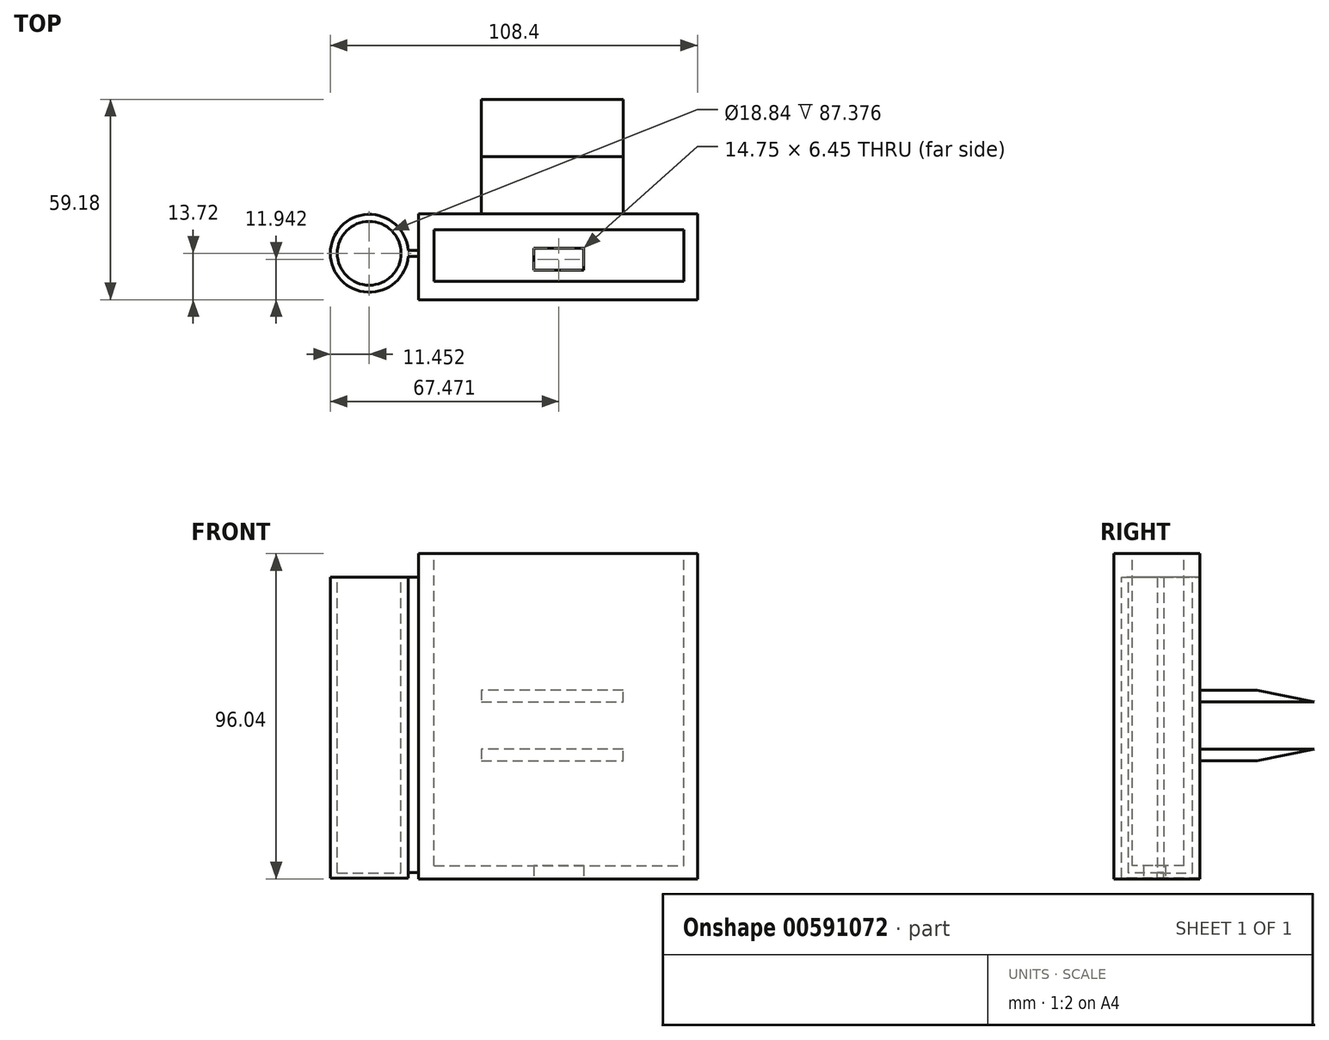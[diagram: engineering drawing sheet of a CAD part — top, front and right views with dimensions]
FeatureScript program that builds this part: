
annotation { "Feature Type Name" : "Feature", "Feature Type Description" : "" }
export const myFeature = defineFeature(function(context is Context, id is Id, definition is map)
    precondition{}
    {
        {
            var Q0;
            Q0=qCreatedBy(makeId("Front.planeOp"),FACE);
            var sketch = newSketch(context, id + "F0", { "sketchPlane" : qUnion([Q0])});
            skLineSegment(sketch, "E0.bottom", {"start": v(-39.73, 43.78) * mm, "end": v(42.68, 43.78) * mm});
            skLineSegment(sketch, "E0.top", {"start": v(-39.73, -52.26) * mm, "end": v(42.68, -52.26) * mm});
            skLineSegment(sketch, "E0.left", {"start": v(-39.73, 43.78) * mm, "end": v(-39.73, -52.26) * mm});
            skLineSegment(sketch, "E0.right", {"start": v(42.68, 43.78) * mm, "end": v(42.68, -52.26) * mm});
            skSolve(sketch);
        }
        {
            var Q0;
            Q0 = qSketchRegion(id + "F0", true);
            extrude(context, id + "F1", {"entities" : qUnion([Q0]), "depth" : 25.4 * mm, "offsetDistance" : 25.4 * mm});
        }
        {
            var Q0;
            Q0=makeQuery(id+"F1.opExtrude","SWEPT_FACE",FACE,{"disambiguationData":[OSD([sQuery(id+"F0.wireOp",EDGE,"E0.bottom")])]});
            var sketch = newSketch(context, id + "F2", { "sketchPlane" : qUnion([Q0])});
            skLineSegment(sketch, "E1.bottom", {"start": v(-35.12, -4.7) * mm, "end": v(38.62, -4.7) * mm});
            skLineSegment(sketch, "E1.top", {"start": v(-35.12, -20) * mm, "end": v(38.62, -20) * mm});
            skLineSegment(sketch, "E1.left", {"start": v(-35.12, -4.7) * mm, "end": v(-35.12, -20) * mm});
            skLineSegment(sketch, "E1.right", {"start": v(38.62, -4.7) * mm, "end": v(38.62, -20) * mm});
            skSolve(sketch);
        }
        {
            var Q0;
            Q0 = qSketchRegion(id + "F2", true);
            extrude(context, id + "F3", {"entities" : qUnion([Q0]), "operationType" : NewBodyOperationType.REMOVE, "oppositeDirection" : true, "depth" : 92.2 * mm, "offsetDistance" : 25.4 * mm});
        }
        {
            var Q0;
            Q0=makeQuery(id+"F1.opExtrude","CAP_FACE",FACE,{"disambiguationData":[OSD([sQuery(id+"F0.wireOp",EDGE,"E0.bottom"),sQuery(id+"F0.wireOp",EDGE,"E0.top"),sQuery(id+"F0.wireOp",EDGE,"E0.left"),sQuery(id+"F0.wireOp",EDGE,"E0.right")])],"isStart":true});
            var sketch = newSketch(context, id + "F4", { "sketchPlane" : qUnion([Q0])});
            skLineSegment(sketch, "E2", {"start": v(-20.74, 3.5) * mm, "end": v(21.1, 3.5) * mm});
            skLineSegment(sketch, "E3", {"start": v(21.1, 3.5) * mm, "end": v(21.1, 0) * mm});
            skLineSegment(sketch, "E4", {"start": v(21.1, 0) * mm, "end": v(-20.74, 0) * mm});
            skLineSegment(sketch, "E5", {"start": v(-20.74, 0) * mm, "end": v(-20.74, 3.5) * mm});
            skLineSegment(sketch, "E6", {"start": v(-20.74, -13.92) * mm, "end": v(21.1, -13.92) * mm});
            skLineSegment(sketch, "E7", {"start": v(21.1, -13.92) * mm, "end": v(21.1, -17.42) * mm});
            skLineSegment(sketch, "E8", {"start": v(21.1, -17.42) * mm, "end": v(-20.74, -17.42) * mm});
            skLineSegment(sketch, "E9", {"start": v(-20.74, -17.42) * mm, "end": v(-20.74, -13.92) * mm});
            skSolve(sketch);
        }
        {
            var Q0;
            Q0 = qSketchRegion(id + "F4", true);
            extrude(context, id + "F5", {"entities" : qUnion([Q0]), "operationType" : NewBodyOperationType.ADD, "depth" : 33.78 * mm, "offsetDistance" : 25.4 * mm});
        }
        {
            var Q0;
            Q0=makeQuery(id+"F5.opExtrude","SWEPT_FACE",FACE,{"disambiguationData":[OSD([sQuery(id+"F4.wireOp",EDGE,"E5")])]});
            var sketch = newSketch(context, id + "F6", { "sketchPlane" : qUnion([Q0])});
            skLineSegment(sketch, "E10", {"start": v(0, 3.5) * mm, "end": v(16.9, 3.5) * mm});
            skLineSegment(sketch, "E11", {"start": v(16.9, 3.5) * mm, "end": v(33.78, 0) * mm});
            skSolve(sketch);
        }
        {
            var Q0;
            {var subQ0=sQuery(id+"F6.wireOp",EDGE,"E11");Q0=makeQuery(id+"F6.imprint","IMPRINT",FACE,{"disambiguationData":[TD([[makeQuery(id+"F6.imprint","IMPRINT",EDGE,{"derivedFrom":subQ0}),1.0]])]});}
            extrude(context, id + "F7", {"entities" : qUnion([Q0]), "operationType" : NewBodyOperationType.REMOVE, "oppositeDirection" : true, "depth" : 58.93 * mm, "offsetDistance" : 25.4 * mm});
        }
        {
            var Q0;
            Q0=makeQuery(id+"F5.opExtrude","SWEPT_FACE",FACE,{"disambiguationData":[OSD([sQuery(id+"F4.wireOp",EDGE,"E9")])]});
            var sketch = newSketch(context, id + "F8", { "sketchPlane" : qUnion([Q0])});
            skLineSegment(sketch, "E12", {"start": v(0, -17.42) * mm, "end": v(16.9, -17.42) * mm});
            skLineSegment(sketch, "E13", {"start": v(16.9, -17.42) * mm, "end": v(33.78, -13.92) * mm});
            skSolve(sketch);
        }
        {
            var Q0;
            {var subQ0=sQuery(id+"F8.wireOp",EDGE,"E13");Q0=makeQuery(id+"F8.imprint","IMPRINT",FACE,{"disambiguationData":[TD([[makeQuery(id+"F8.imprint","IMPRINT",EDGE,{"derivedFrom":subQ0}),-1.0]])]});}
            extrude(context, id + "F9", {"entities" : qUnion([Q0]), "operationType" : NewBodyOperationType.REMOVE, "oppositeDirection" : true, "depth" : 50.3 * mm, "offsetDistance" : 25.4 * mm});
        }
        {
            var Q0;
            Q0=makeQuery(id+"F1.opExtrude","SWEPT_FACE",FACE,{"disambiguationData":[OSD([sQuery(id+"F0.wireOp",EDGE,"E0.top")])]});
            var sketch = newSketch(context, id + "F10", { "sketchPlane" : qUnion([Q0])});
            skLineSegment(sketch, "E14.bottom", {"start": v(-5.62, 16.68) * mm, "end": v(9.13, 16.68) * mm});
            skLineSegment(sketch, "E14.top", {"start": v(-5.62, 10.23) * mm, "end": v(9.13, 10.23) * mm});
            skLineSegment(sketch, "E14.left", {"start": v(-5.62, 16.68) * mm, "end": v(-5.62, 10.23) * mm});
            skLineSegment(sketch, "E14.right", {"start": v(9.13, 16.68) * mm, "end": v(9.13, 10.23) * mm});
            skSolve(sketch);
        }
        {
            var Q0;
            Q0=makeQuery(id+"F10.imprint","IMPRINT",FACE,{"disambiguationData":[TD([[makeQuery(id+"F10.imprint","IMPRINT",EDGE,{"derivedFrom":sQuery(id+"F10.wireOp",EDGE,"E14.bottom")}),-1.0]])]});
            extrude(context, id + "F11", {"entities" : qUnion([Q0]), "operationType" : NewBodyOperationType.REMOVE, "oppositeDirection" : true, "depth" : 25.4 * mm, "offsetDistance" : 25.4 * mm});
        }
        {
            var Q0;
            Q0=makeQuery(id+"F1.opExtrude","SWEPT_FACE",FACE,{"disambiguationData":[OSD([sQuery(id+"F0.wireOp",EDGE,"E0.left")])]});
            var sketch = newSketch(context, id + "F12", { "sketchPlane" : qUnion([Q0])});
            skLineSegment(sketch, "E15.bottom", {"start": v(10.76, 36.85) * mm, "end": v(12.6, 36.85) * mm});
            skLineSegment(sketch, "E15.top", {"start": v(10.76, -50.35) * mm, "end": v(12.6, -50.35) * mm});
            skLineSegment(sketch, "E15.left", {"start": v(10.76, 36.85) * mm, "end": v(10.76, -50.35) * mm});
            skLineSegment(sketch, "E15.right", {"start": v(12.6, 36.85) * mm, "end": v(12.6, -50.35) * mm});
            skSolve(sketch);
        }
        {
            var Q0;
            Q0 = qSketchRegion(id + "F12", true);
            extrude(context, id + "F13", {"entities" : qUnion([Q0]), "operationType" : NewBodyOperationType.ADD, "depth" : 3.05 * mm, "offsetDistance" : 25.4 * mm});
        }
        {
            var Q0;
            Q0=makeQuery(id+"F13.opExtrude","SWEPT_FACE",FACE,{"disambiguationData":[OSD([sQuery(id+"F12.wireOp",EDGE,"E15.bottom")])]});
            var sketch = newSketch(context, id + "F14", { "sketchPlane" : qUnion([Q0])});
            skCircle(sketch, "E16", {"center": v(-54.23, -11.68) * mm, "radius": 11.5 * mm});
            skPoint(sketch, "E16.first.point", {"position": v(-42.78, -10.76) * mm});
            skPoint(sketch, "E16.second.point", {"position": v(-42.78, -12.6) * mm});
            skPoint(sketch, "E16.third.point", {"position": v(-65.17, -15.2) * mm});
            skCircle(sketch, "E17", {"center": v(-54.27, -11.68) * mm, "radius": 9.42 * mm});
            skPoint(sketch, "E17.first.point", {"position": v(-44.9, -10.76) * mm});
            skPoint(sketch, "E17.second.point", {"position": v(-44.9, -12.6) * mm});
            skPoint(sketch, "E17.third.point", {"position": v(-60.93, -18.34) * mm});
            skSolve(sketch);
        }
        {
            var Q0;
            Q0=makeQuery(id+"F14.imprint","IMPRINT",FACE,{"disambiguationData":[TD([[makeQuery(id+"F14.imprint","IMPRINT",EDGE,{"derivedFrom":sQuery(id+"F14.wireOp",EDGE,"E17")}),-1.0]])]});
            extrude(context, id + "F15", {"entities" : qUnion([Q0]), "operationType" : NewBodyOperationType.ADD, "oppositeDirection" : true, "depth" : 88.9 * mm, "offsetDistance" : 25.4 * mm});
        }
        {
            var Q0;
            Q0=makeQuery(id+"F15.opExtrude","CAP_FACE",FACE,{"disambiguationData":[OSD([sQuery(id+"F12.wireOp",EDGE,"E15.bottom"),sQuery(id+"F14.wireOp",EDGE,"E16"),sQuery(id+"F14.wireOp",EDGE,"E17")])],"isStart":false});
            var sketch = newSketch(context, id + "F16", { "sketchPlane" : qUnion([Q0])});
            skCircle(sketch, "E18", {"center": v(-54.27, 11.68) * mm, "radius": 9.42 * mm});
            skPoint(sketch, "E18.first.point", {"position": v(-46.01, 7.13) * mm});
            skPoint(sketch, "E18.second.point", {"position": v(-62.62, 16.04) * mm});
            skPoint(sketch, "E18.third.point", {"position": v(-57.46, 2.82) * mm});
            skSolve(sketch);
        }
        {
            var Q0;
            Q0 = qSketchRegion(id + "F16", true);
            extrude(context, id + "F17", {"entities" : qUnion([Q0]), "operationType" : NewBodyOperationType.ADD, "oppositeDirection" : true, "depth" : 1.52 * mm, "offsetDistance" : 25.4 * mm});
        }
    });
